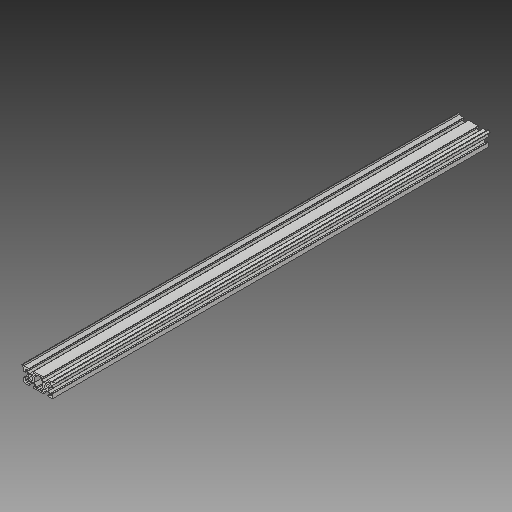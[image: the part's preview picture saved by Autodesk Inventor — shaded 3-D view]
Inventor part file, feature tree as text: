
AUTODESK INVENTOR PART (.ipt)
format: ipt  version: 2018 (Build 220112000, 112)  size: 230,912 bytes
history: native  units: mm
features: other x2, extrude x1, sketch x1, reference x1
ambient origin geometry x8: Origin, YZ Plane, XZ Plane, XY Plane, X Axis, Y Axis, Z Axis, Center Point
bodies: Solid1 (feature_tree)
feature tree (5):
  extrude  "Extrusion1"  [1 undecoded]
  sketch  "Sketch1"  dims[d0=600.0mm d1=0.0mm]
  reference  "Reference1"
  other  "Assembly3"
  other  "Makerslide Default 300mm:1"
note: 1 required parameter value undecoded (feature->parameter linkage not recoverable at this tier; creation-order binding heuristic only, values carry confidence <= 0.55)
